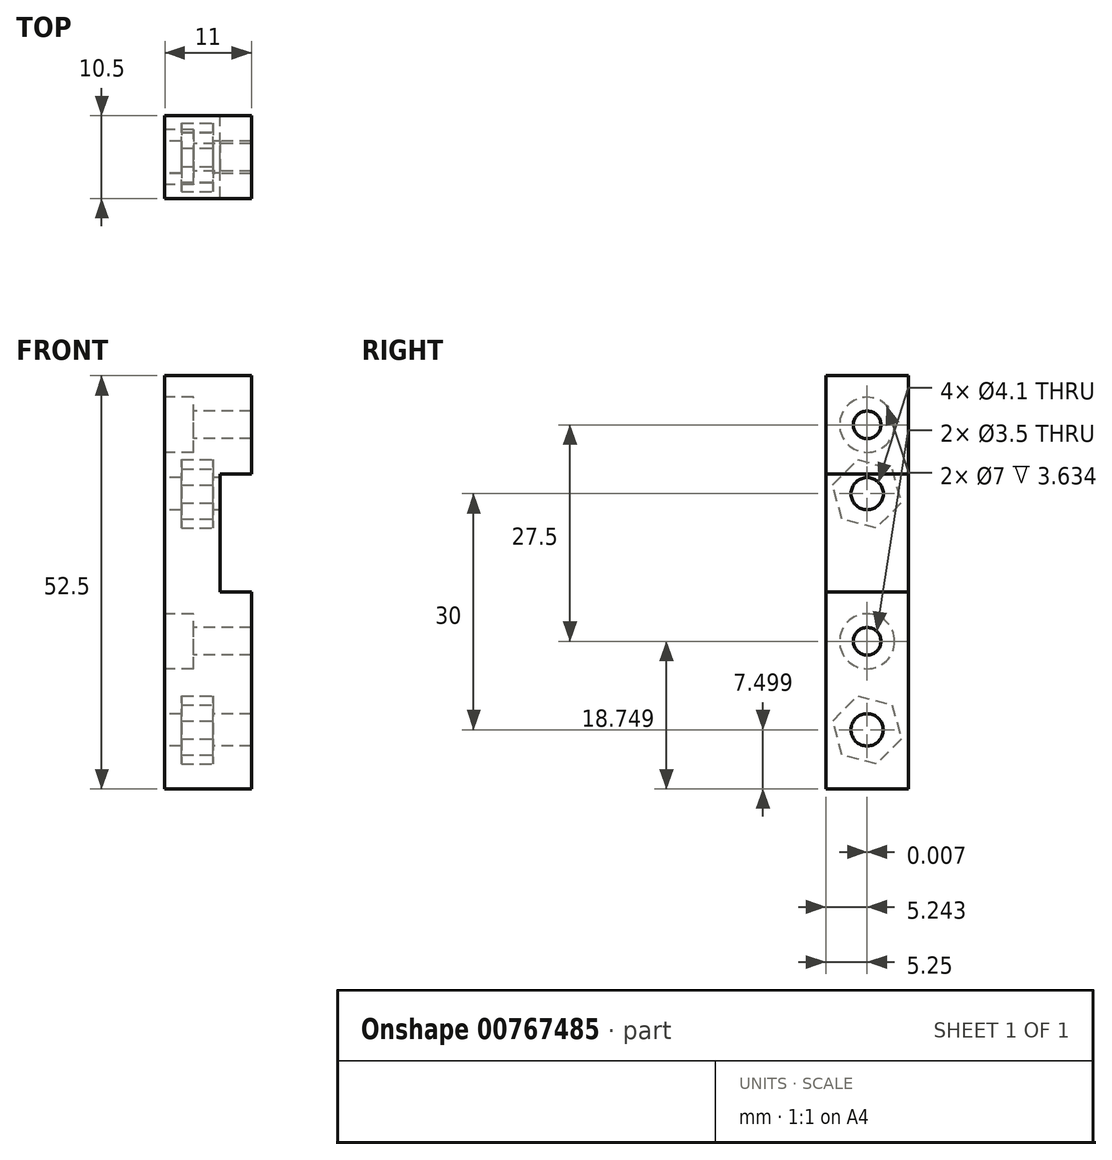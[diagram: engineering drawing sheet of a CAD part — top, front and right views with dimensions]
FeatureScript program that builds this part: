
annotation { "Feature Type Name" : "Feature", "Feature Type Description" : "" }
export const myFeature = defineFeature(function(context is Context, id is Id, definition is map)
    precondition{}
    {
        {
            var Q0;
            Q0=qCreatedBy(makeId("Front.planeOp"),FACE);
            var sketch = newSketch(context, id + "F0", { "sketchPlane" : qUnion([Q0])});
            skLineSegment(sketch, "E0.bottom", {"start": v(1.37, 24.14) * mm, "end": v(12.37, 24.14) * mm});
            skLineSegment(sketch, "E0.top", {"start": v(1.37, -28.36) * mm, "end": v(12.37, -28.36) * mm});
            skLineSegment(sketch, "E0.left", {"start": v(1.37, 24.14) * mm, "end": v(1.37, -28.36) * mm});
            skLineSegment(sketch, "E0.right", {"start": v(12.37, 24.14) * mm, "end": v(12.37, 11.64) * mm});
            skLineSegment(sketch, "E1.bottom", {"start": v(12.37, 24.14) * mm, "end": v(9.37, 24.14) * mm});
            skLineSegment(sketch, "E1.top", {"start": v(17.37, 11.64) * mm, "end": v(8.37, 11.64) * mm});
            skLineSegment(sketch, "E2.bottom", {"start": v(8.37, 11.64) * mm, "end": v(12.37, 11.64) * mm});
            skLineSegment(sketch, "E2.top", {"start": v(8.37, -3.36) * mm, "end": v(12.37, -3.36) * mm});
            skLineSegment(sketch, "E2.left", {"start": v(8.37, 11.64) * mm, "end": v(8.37, -3.36) * mm});
            skLineSegment(sketch, "E3.trimOffspring", {"start": v(12.37, -3.36) * mm, "end": v(12.37, -28.36) * mm});
            skSolve(sketch);
        }
        {
            var Q0;
            Q0=makeQuery(id+"F0.imprint","IMPRINT",FACE,{"disambiguationData":[TD([[makeQuery(id+"F0.imprint","IMPRINT",EDGE,{"derivedFrom":sQuery(id+"F0.wireOp",EDGE,"E0.bottom")}),-1.0]])]});
            extrude(context, id + "F1", {"entities" : qUnion([Q0]), "depth" : 10.5 * mm, "offsetDistance" : 25 * mm});
        }
        {
            var Q0;
            Q0=qCreatedBy(makeId("Right.planeOp"),FACE);
            var sketch = newSketch(context, id + "F2", { "sketchPlane" : qUnion([Q0])});
            skCircle(sketch, "E4", {"center": v(-5.25, 17.89) * mm, "radius": 1.75 * mm});
            skCircle(sketch, "E5", {"center": v(-5.25, -9.61) * mm, "radius": 1.75 * mm});
            skCircle(sketch, "E6", {"center": v(-5.25, 17.89) * mm, "radius": 3.5 * mm});
            skCircle(sketch, "E7", {"center": v(-5.25, -9.61) * mm, "radius": 3.5 * mm});
            skCircle(sketch, "E8", {"center": v(-5.26, -20.86) * mm, "radius": 2.05 * mm});
            skCircle(sketch, "E9", {"center": v(-5.25, 9.14) * mm, "radius": 2.05 * mm});
            skSolve(sketch);
        }
        {
            var Q0;
            Q0=makeQuery(id+"F2.imprint","IMPRINT",FACE,{"disambiguationData":[TD([[makeQuery(id+"F2.imprint","IMPRINT",EDGE,{"derivedFrom":sQuery(id+"F2.wireOp",EDGE,"E5")}),1.0]])]});
            var Q1;
            Q1=makeQuery(id+"F2.imprint","IMPRINT",FACE,{"disambiguationData":[TD([[makeQuery(id+"F2.imprint","IMPRINT",EDGE,{"derivedFrom":sQuery(id+"F2.wireOp",EDGE,"E4")}),1.0]])]});
            var Q2;
            Q2=sQuery(id+"F2.wireOp",EDGE,"E5");
            var Q3;
            Q3=sQuery(id+"F2.wireOp",EDGE,"E4");
            extrude(context, id + "F3", {"entities" : qUnion([Q0, Q1]), "operationType" : NewBodyOperationType.REMOVE, "surfaceEntities" : qUnion([Q2, Q3]), "oppositeDirection" : true, "depth" : -50 * mm, "offsetDistance" : 25 * mm});
        }
        {
            var Q0;
            Q0=makeQuery(id+"F2.imprint","IMPRINT",FACE,{"disambiguationData":[TD([[makeQuery(id+"F2.imprint","IMPRINT",EDGE,{"derivedFrom":sQuery(id+"F2.wireOp",EDGE,"E5")}),-1.0]])]});
            var Q1;
            Q1=makeQuery(id+"F2.imprint","IMPRINT",FACE,{"disambiguationData":[TD([[makeQuery(id+"F2.imprint","IMPRINT",EDGE,{"derivedFrom":sQuery(id+"F2.wireOp",EDGE,"E4")}),-1.0]])]});
            var Q2;
            Q2=sQuery(id+"F2.wireOp",EDGE,"E6");
            var Q3;
            Q3=sQuery(id+"F2.wireOp",EDGE,"E7");
            extrude(context, id + "F4", {"entities" : qUnion([Q0, Q1]), "operationType" : NewBodyOperationType.REMOVE, "surfaceEntities" : qUnion([Q2, Q3]), "oppositeDirection" : true, "depth" : -5 * mm, "offsetDistance" : 25 * mm});
        }
        {
            var Q0;
            Q0=makeQuery(id+"F2.imprint","IMPRINT",FACE,{"disambiguationData":[TD([[makeQuery(id+"F2.imprint","IMPRINT",EDGE,{"derivedFrom":sQuery(id+"F2.wireOp",EDGE,"E8")}),1.0]])]});
            var Q1;
            Q1=makeQuery(id+"F2.imprint","IMPRINT",FACE,{"disambiguationData":[TD([[makeQuery(id+"F2.imprint","IMPRINT",EDGE,{"derivedFrom":sQuery(id+"F2.wireOp",EDGE,"E9")}),1.0]])]});
            var Q2;
            Q2=sQuery(id+"F2.wireOp",EDGE,"E9");
            var Q3;
            Q3=sQuery(id+"F2.wireOp",EDGE,"E8");
            extrude(context, id + "F5", {"entities" : qUnion([Q0, Q1]), "operationType" : NewBodyOperationType.REMOVE, "surfaceEntities" : qUnion([Q2, Q3]), "oppositeDirection" : true, "depth" : -20 * mm, "offsetDistance" : 25 * mm});
        }
        {
            var Q0;
            Q0=qCreatedBy(makeId("Right.planeOp"),FACE);
            cPlane(context, id + "F6", {"entities" : qUnion([Q0]), "cplaneType" : CPlaneType.OFFSET, "offset" : 7.5 * mm, "width" : 150 * mm, "height" : 150 * mm});
        }
        {
            var Q0;
            Q0=qCreatedBy(id+"F6.planeOp",FACE);
            var sketch = newSketch(context, id + "F7", { "sketchPlane" : qUnion([Q0])});
            skCircle(sketch, "E10.cCircle", {"center": v(-5.26, -20.87) * mm, "radius": 3.9 * mm, "construction": true});
            skLineSegment(sketch, "E10.0", {"start": v(-9.61, -19.73) * mm, "end": v(-6.45, -16.53) * mm});
            skLineSegment(sketch, "E10.1", {"start": v(-6.45, -16.53) * mm, "end": v(-2.1, -17.67) * mm});
            skLineSegment(sketch, "E10.2", {"start": v(-2.1, -17.67) * mm, "end": v(-0.9, -22) * mm});
            skLineSegment(sketch, "E10.3", {"start": v(-0.9, -22) * mm, "end": v(-4.07, -25.2) * mm});
            skLineSegment(sketch, "E10.4", {"start": v(-4.07, -25.2) * mm, "end": v(-8.42, -24.07) * mm});
            skLineSegment(sketch, "E10.5", {"start": v(-8.42, -24.07) * mm, "end": v(-9.61, -19.73) * mm});
            skPoint(sketch, "E10.0.midPoint", {"position": v(-8.03, -18.13) * mm});
            skCircle(sketch, "E11.cCircle", {"center": v(-5.28, 9.1) * mm, "radius": 3.9 * mm, "construction": true});
            skLineSegment(sketch, "E11.0", {"start": v(-9.63, 10.26) * mm, "end": v(-6.46, 13.45) * mm});
            skLineSegment(sketch, "E11.1", {"start": v(-6.46, 13.45) * mm, "end": v(-2.11, 12.3) * mm});
            skLineSegment(sketch, "E11.2", {"start": v(-2.11, 12.3) * mm, "end": v(-0.93, 7.96) * mm});
            skLineSegment(sketch, "E11.3", {"start": v(-0.93, 7.96) * mm, "end": v(-4.1, 4.77) * mm});
            skLineSegment(sketch, "E11.4", {"start": v(-4.1, 4.77) * mm, "end": v(-8.45, 5.91) * mm});
            skLineSegment(sketch, "E11.5", {"start": v(-8.45, 5.91) * mm, "end": v(-9.63, 10.26) * mm});
            skPoint(sketch, "E11.0.midPoint", {"position": v(-8.05, 11.85) * mm});
            skSolve(sketch);
        }
        {
            var Q0;
            Q0 = qSketchRegion(id + "F7", true);
            extrude(context, id + "F8", {"entities" : qUnion([Q0]), "operationType" : NewBodyOperationType.REMOVE, "oppositeDirection" : true, "depth" : 4 * mm, "offsetDistance" : 25 * mm});
        }
    });
